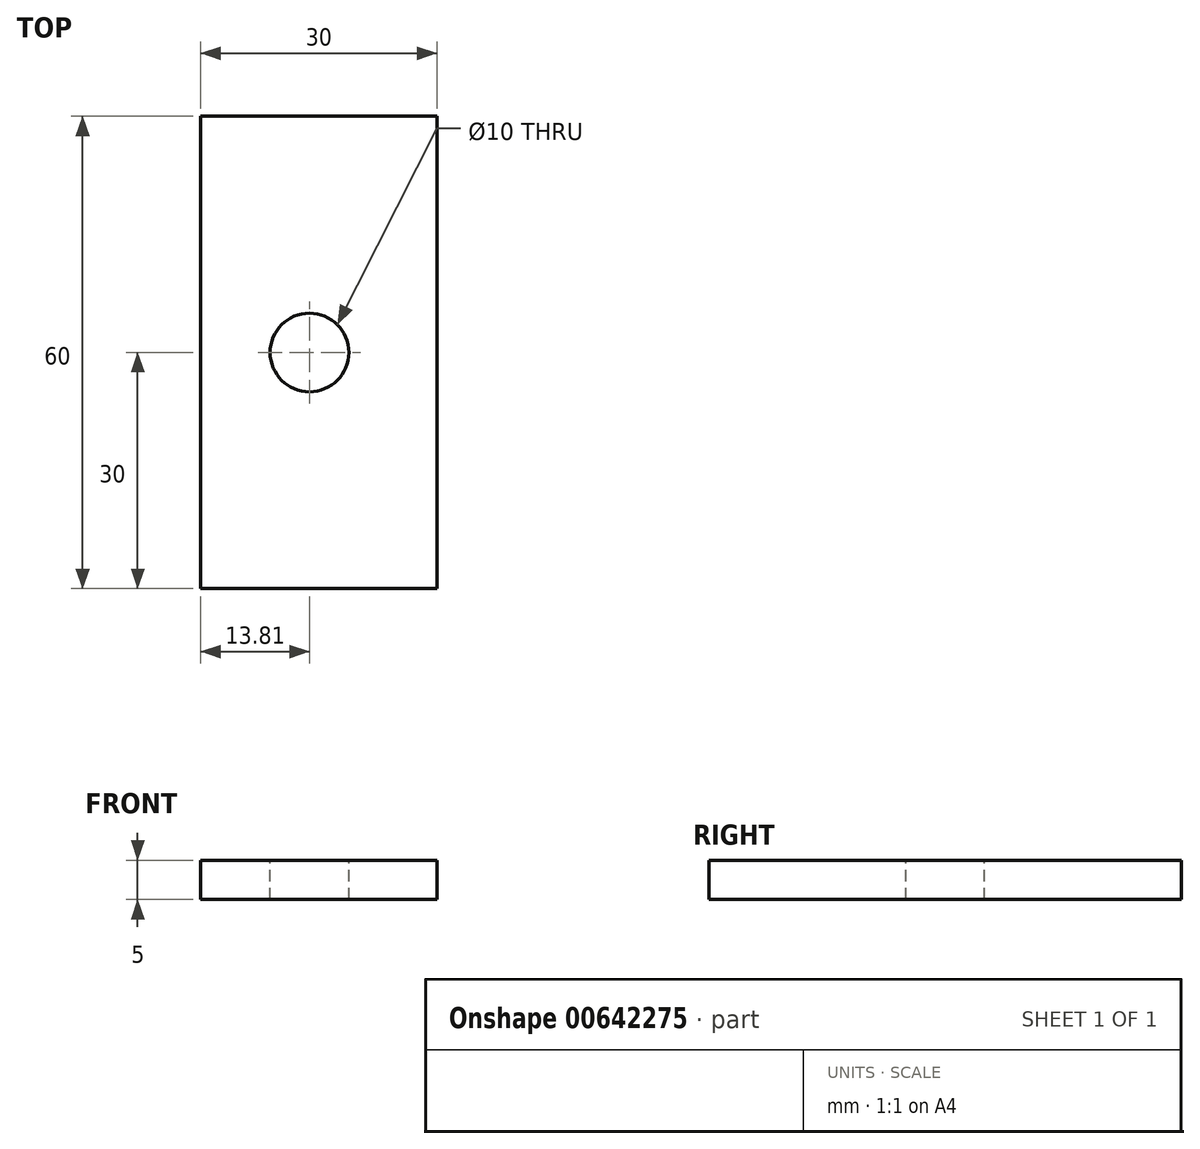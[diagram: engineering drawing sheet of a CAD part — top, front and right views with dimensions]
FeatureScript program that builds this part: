
annotation { "Feature Type Name" : "Feature", "Feature Type Description" : "" }
export const myFeature = defineFeature(function(context is Context, id is Id, definition is map)
    precondition{}
    {
        {
            var Q0;
            Q0=qCreatedBy(makeId("Front.planeOp"),FACE);
            var sketch = newSketch(context, id + "F0", { "sketchPlane" : qUnion([Q0])});
            skLineSegment(sketch, "E0.bottom", {"start": v(16.2, -2.5) * mm, "end": v(-13.8, -2.5) * mm});
            skLineSegment(sketch, "E0.top", {"start": v(16.2, 2.5) * mm, "end": v(-13.8, 2.5) * mm});
            skLineSegment(sketch, "E0.left", {"start": v(16.2, -2.5) * mm, "end": v(16.2, 2.5) * mm});
            skLineSegment(sketch, "E0.right", {"start": v(-13.8, -2.5) * mm, "end": v(-13.8, 2.5) * mm});
            skPoint(sketch, "E0.middle", {"position": v(1.2, 0) * mm});
            skSolve(sketch);
        }
        {
            var Q0;
            Q0=makeQuery(id+"F0.imprint","IMPRINT",FACE,{"disambiguationData":[TD([[makeQuery(id+"F0.imprint","IMPRINT",EDGE,{"derivedFrom":sQuery(id+"F0.wireOp",EDGE,"E0.bottom")}),-1.0]])]});
            extrude(context, id + "F1", {"entities" : qUnion([Q0]), "depth" : 60 * mm, "offsetDistance" : 25 * mm});
        }
        {
            var Q0;
            Q0=makeQuery(id+"F1.opExtrude","SWEPT_FACE",FACE,{"disambiguationData":[OSD([sQuery(id+"F0.wireOp",EDGE,"E0.top")])]});
            var sketch = newSketch(context, id + "F2", { "sketchPlane" : qUnion([Q0])});
            skPoint(sketch, "E1", {"position": v(0, -30) * mm});
            skPoint(sketch, "E1.positionSnap0", {"position": v(-13.8, -30) * mm});
            skSolve(sketch);
        }
        {
            var Q0;
            Q0=sQuery(id+"F2.wireOp",VERTEX,"E1");
            var Q1;
            Q1=makeQuery(id+"F1.opExtrude","SWEPT_BODY",BODY,{"disambiguationData":[OSD([sQuery(id+"F0.wireOp",EDGE,"E0.bottom"),sQuery(id+"F0.wireOp",EDGE,"E0.top"),sQuery(id+"F0.wireOp",EDGE,"E0.left"),sQuery(id+"F0.wireOp",EDGE,"E0.right")])]});
            hole(context, id + "F3", {"style" : HoleStyle.SIMPLE, "endStyle" : HoleEndStyle.THROUGH, "holeDiameter" : 10 * mm, "majorDiameter" : 5 * mm, "isTappedThrough" : true, "tappedDepth" : 12 * mm, "tapClearance" : 3, "locations" : qUnion([Q0]), "scope" : qUnion([Q1])});
        }
    });
